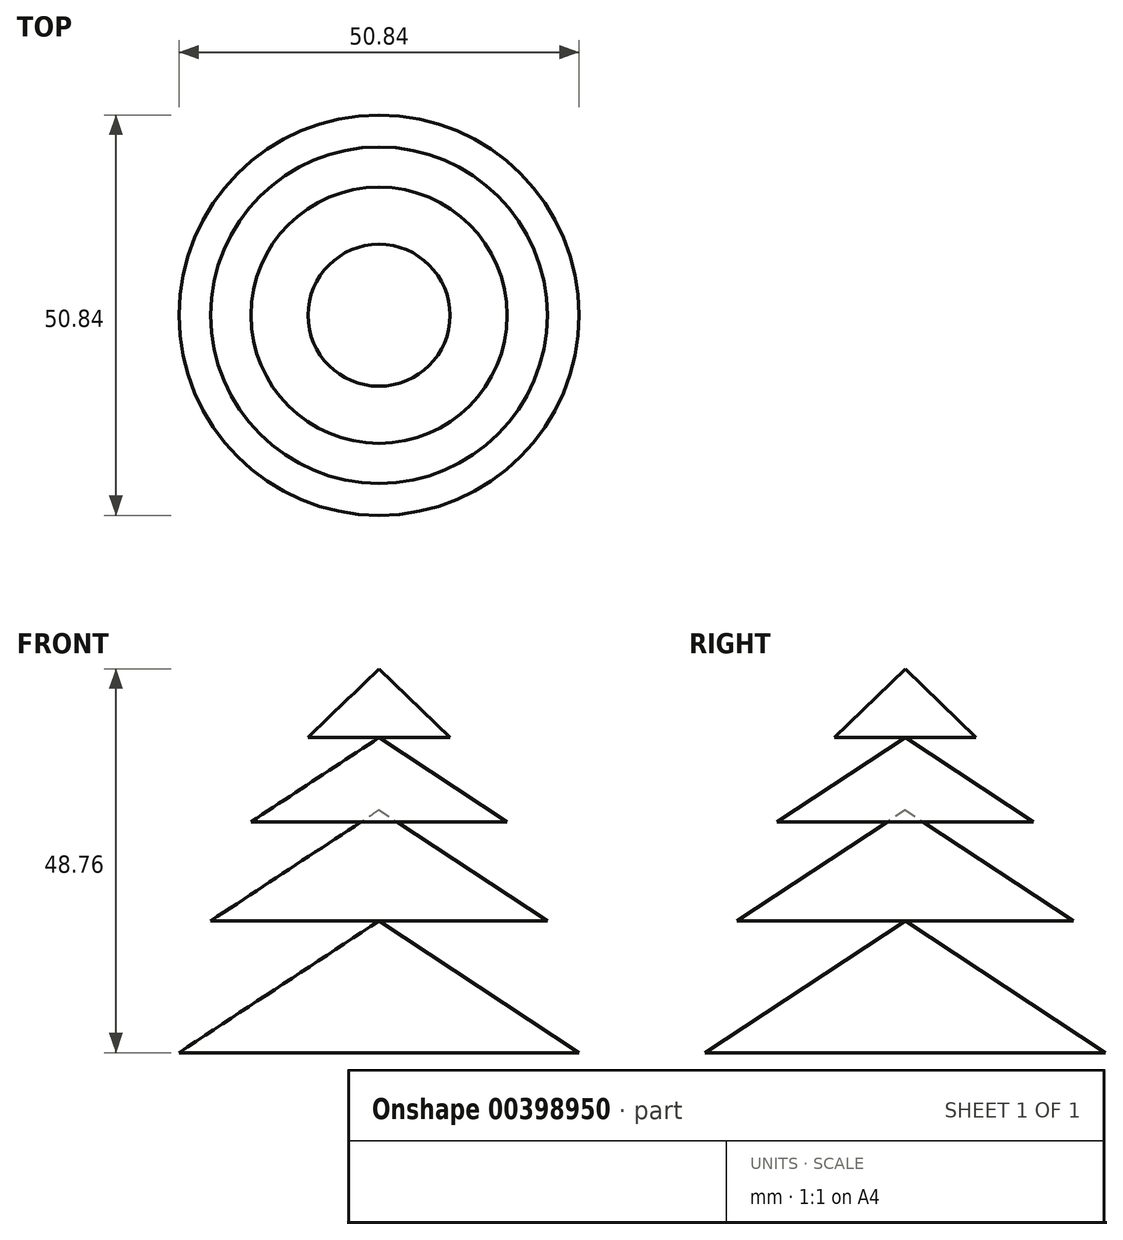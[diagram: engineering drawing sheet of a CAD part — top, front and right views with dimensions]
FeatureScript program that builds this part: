
annotation { "Feature Type Name" : "Feature", "Feature Type Description" : "" }
export const myFeature = defineFeature(function(context is Context, id is Id, definition is map)
    precondition{}
    {
        {
            var Q0;
            Q0=qCreatedBy(makeId("Front.planeOp"),FACE);
            var sketch = newSketch(context, id + "F0", { "sketchPlane" : qUnion([Q0])});
            skLineSegment(sketch, "E0", {"start": v(0, 0) * mm, "end": v(0, 77.27) * mm});
            skSolve(sketch);
        }
        {
            var Q0;
            Q0=qCreatedBy(makeId("Front.planeOp"),FACE);
            var sketch = newSketch(context, id + "F1", { "sketchPlane" : qUnion([Q0])});
            skLineSegment(sketch, "E1", {"start": v(0, 0) * mm, "end": v(-25.42, 0) * mm});
            skLineSegment(sketch, "E2", {"start": v(-25.42, 0) * mm, "end": v(0, 16.74) * mm});
            skLineSegment(sketch, "E3", {"start": v(0, 16.74) * mm, "end": v(-21.37, 16.74) * mm});
            skLineSegment(sketch, "E4", {"start": v(-21.37, 16.74) * mm, "end": v(0, 30.82) * mm});
            skLineSegment(sketch, "E5", {"start": v(0, 30.82) * mm, "end": v(-16.27, 29.32) * mm});
            skLineSegment(sketch, "E6", {"start": v(-16.27, 29.32) * mm, "end": v(0, 40.03) * mm});
            skLineSegment(sketch, "E7", {"start": v(0, 40.03) * mm, "end": v(-9.02, 40.03) * mm});
            skLineSegment(sketch, "E8", {"start": v(-9.02, 40.03) * mm, "end": v(0, 48.76) * mm});
            skSolve(sketch);
        }
        {
            var Q0;
            Q0=sQuery(id+"F1.wireOp",EDGE,"E8");
            var Q1;
            Q1=sQuery(id+"F0.wireOp",EDGE,"E0");
            revolve(context, id + "F2", {"bodyType" : ToolBodyType.SURFACE, "surfaceEntities" : qUnion([Q0]), "axis" : qUnion([Q1]), "revolveType" : RevolveType.FULL});
        }
        {
            var Q0;
            Q0=sQuery(id+"F1.wireOp",EDGE,"E6");
            var Q1;
            Q1=sQuery(id+"F0.wireOp",EDGE,"E0");
            revolve(context, id + "F3", {"bodyType" : ToolBodyType.SURFACE, "surfaceEntities" : qUnion([Q0]), "axis" : qUnion([Q1]), "revolveType" : RevolveType.FULL});
        }
        {
            var Q0;
            Q0=sQuery(id+"F1.wireOp",EDGE,"E4");
            var Q1;
            Q1=sQuery(id+"F0.wireOp",EDGE,"E0");
            revolve(context, id + "F4", {"bodyType" : ToolBodyType.SURFACE, "surfaceEntities" : qUnion([Q0]), "axis" : qUnion([Q1]), "revolveType" : RevolveType.FULL});
        }
        {
            var Q0;
            Q0=sQuery(id+"F1.wireOp",EDGE,"E2");
            var Q1;
            Q1=sQuery(id+"F0.wireOp",EDGE,"E0");
            revolve(context, id + "F5", {"bodyType" : ToolBodyType.SURFACE, "surfaceEntities" : qUnion([Q0]), "axis" : qUnion([Q1]), "revolveType" : RevolveType.FULL});
        }
    });
